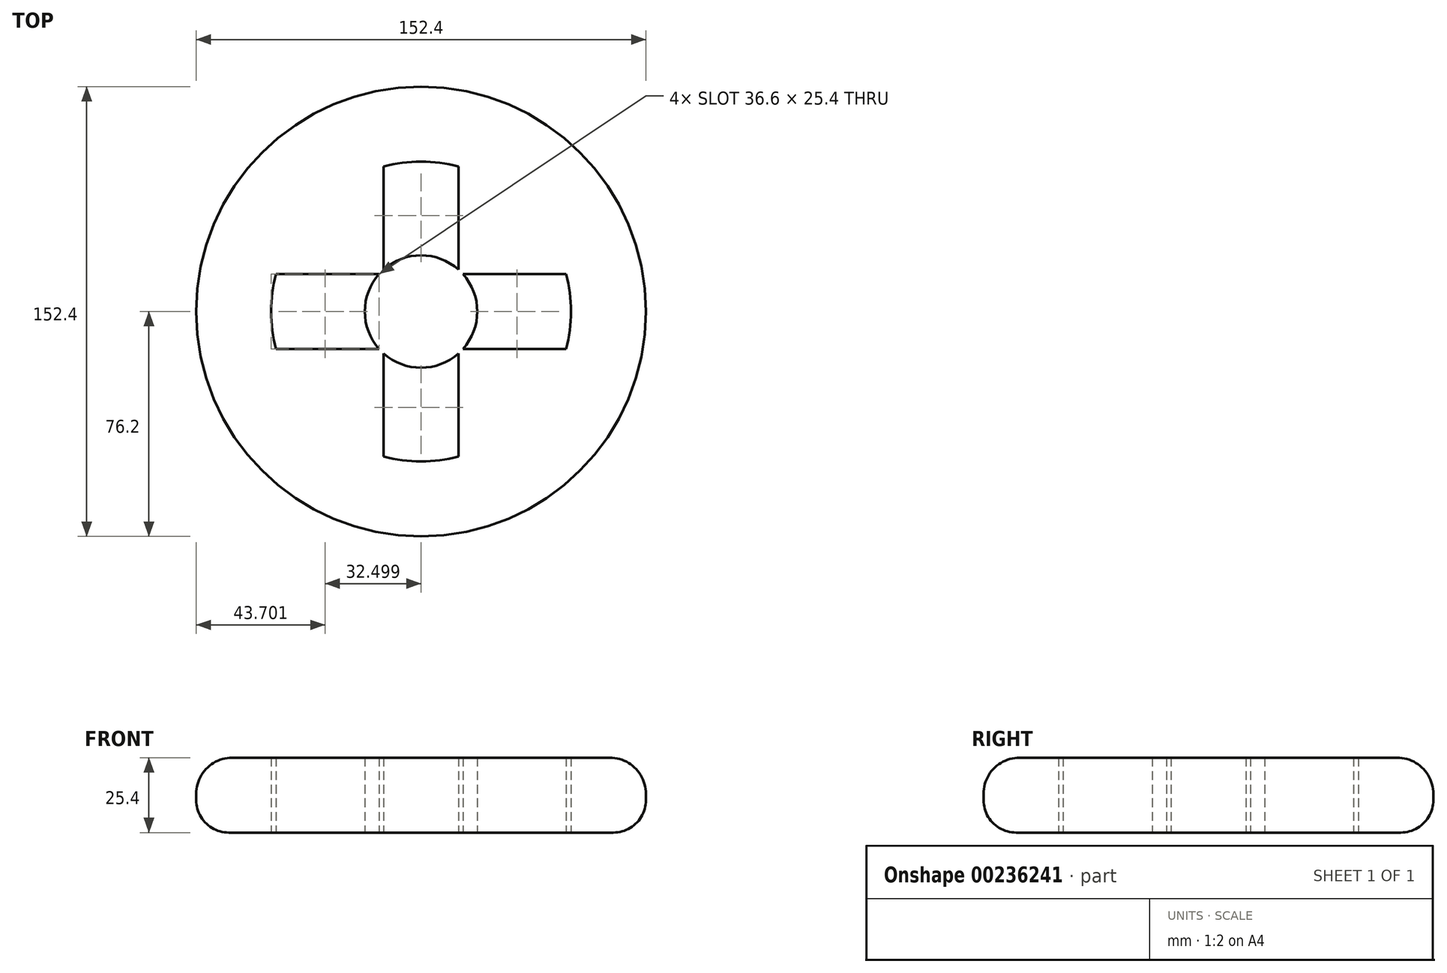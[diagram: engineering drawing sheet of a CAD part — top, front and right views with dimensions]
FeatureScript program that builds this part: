
annotation { "Feature Type Name" : "Feature", "Feature Type Description" : "" }
export const myFeature = defineFeature(function(context is Context, id is Id, definition is map)
    precondition{}
    {
        {
            var Q0;
            Q0=qCreatedBy(makeId("Top.planeOp"),FACE);
            var sketch = newSketch(context, id + "F0", { "sketchPlane" : qUnion([Q0])});
            skCircle(sketch, "E0", {"center": v(0, 0) * mm, "radius": 76.2 * mm});
            skCircle(sketch, "E1", {"center": v(0, 0) * mm, "radius": 50.8 * mm});
            skArc(sketch, "E2", {"start": v(14.2, -12.7) * mm, "mid": v(19.05, 0) * mm, "end": v(14.2, 12.7) * mm});
            skLineSegment(sketch, "E3", {"start": v(0, -50.8) * mm, "end": v(0, -12.7) * mm});
            skLineSegment(sketch, "E4.0", {"start": v(12.7, -49.19) * mm, "end": v(12.7, 0) * mm});
            skLineSegment(sketch, "E5.0", {"start": v(-12.7, -49.19) * mm, "end": v(-12.7, 0) * mm});
            skLineSegment(sketch, "E6", {"start": v(-12.7, 0) * mm, "end": v(-50.8, 0) * mm});
            skLineSegment(sketch, "E7", {"start": v(12.7, 0) * mm, "end": v(50.8, 0) * mm});
            skLineSegment(sketch, "E8", {"start": v(0, 12.7) * mm, "end": v(0, 50.8) * mm});
            skLineSegment(sketch, "E9.0", {"start": v(-12.7, 12.7) * mm, "end": v(-49.19, 12.7) * mm});
            skLineSegment(sketch, "E10.0", {"start": v(0, -12.7) * mm, "end": v(-49.19, -12.7) * mm});
            skLineSegment(sketch, "E10.1", {"start": v(0, -12.7) * mm, "end": v(49.19, -12.7) * mm});
            skLineSegment(sketch, "E11.0", {"start": v(0, 12.7) * mm, "end": v(49.19, 12.7) * mm});
            skLineSegment(sketch, "E12.0", {"start": v(12.7, 0) * mm, "end": v(12.7, 49.19) * mm});
            skLineSegment(sketch, "E13.0", {"start": v(-12.7, 12.7) * mm, "end": v(-12.7, 49.19) * mm});
            skLineSegment(sketch, "E14", {"start": v(-12.7, 12.7) * mm, "end": v(0, 12.7) * mm});
            skLineSegment(sketch, "E15", {"start": v(-12.7, 12.7) * mm, "end": v(-12.7, 0) * mm});
            skArc(sketch, "E16.trimOffspring", {"start": v(12.7, 14.2) * mm, "mid": v(0, 19.05) * mm, "end": v(-12.7, 14.2) * mm});
            skArc(sketch, "E17.trimOffspring", {"start": v(-14.2, 12.7) * mm, "mid": v(-19.05, 0) * mm, "end": v(-14.2, -12.7) * mm});
            skArc(sketch, "E18.trimOffspring", {"start": v(-12.7, -14.2) * mm, "mid": v(0, -19.05) * mm, "end": v(12.7, -14.2) * mm});
            skPoint(sketch, "E19.orphan", {"position": v(0, -76.2) * mm});
            skSolve(sketch);
        }
        {
            var Q0;
            Q0 = qSketchRegion(id + "F0", true);
            var Q1;
            {var subQ0=sQuery(id+"F0.wireOp",EDGE,"E4.0");var subQ1=sQuery(id+"F0.wireOp",EDGE,"E1");var subQ2=makeQuery(id+"F0.imprint","INTERSECT",VERTEX,{"derivedFrom":[subQ1,subQ0]});Q1=makeQuery(id+"F0.imprint","IMPRINT",FACE,{"disambiguationData":[TD([[makeQuery(id+"F0.imprint","IMPRINT",EDGE,{"disambiguationData":[TD([[subQ2,-1.0]])],"derivedFrom":subQ1}),1.0]])]});}
            var Q2;
            {var subQ0=sQuery(id+"F0.wireOp",EDGE,"E10.0");var subQ1=sQuery(id+"F0.wireOp",EDGE,"E1");var subQ2=makeQuery(id+"F0.imprint","INTERSECT",VERTEX,{"derivedFrom":[subQ1,subQ0]});Q2=makeQuery(id+"F0.imprint","IMPRINT",FACE,{"disambiguationData":[TD([[makeQuery(id+"F0.imprint","IMPRINT",EDGE,{"disambiguationData":[TD([[subQ2,-1.0]])],"derivedFrom":subQ1}),1.0]])]});}
            var Q3;
            {var subQ0=sQuery(id+"F0.wireOp",EDGE,"E13.0");var subQ1=sQuery(id+"F0.wireOp",EDGE,"E1");var subQ2=makeQuery(id+"F0.imprint","INTERSECT",VERTEX,{"derivedFrom":[subQ1,subQ0]});Q3=makeQuery(id+"F0.imprint","IMPRINT",FACE,{"disambiguationData":[TD([[makeQuery(id+"F0.imprint","IMPRINT",EDGE,{"disambiguationData":[TD([[subQ2,-1.0]])],"derivedFrom":subQ1}),1.0]])]});}
            var Q4;
            {var subQ0=sQuery(id+"F0.wireOp",EDGE,"E11.0");var subQ1=sQuery(id+"F0.wireOp",EDGE,"E1");var subQ2=makeQuery(id+"F0.imprint","INTERSECT",VERTEX,{"derivedFrom":[subQ1,subQ0]});Q4=makeQuery(id+"F0.imprint","IMPRINT",FACE,{"disambiguationData":[TD([[makeQuery(id+"F0.imprint","IMPRINT",EDGE,{"disambiguationData":[TD([[subQ2,-1.0]])],"derivedFrom":subQ1}),1.0]])]});}
            var Q5;
            {var subQ3=sQuery(id+"F0.wireOp",EDGE,"E10.1");var subQ5=sQuery(id+"F0.wireOp",EDGE,"E4.0");var subQ6=makeQuery(id+"F0.imprint","INTERSECT",VERTEX,{"derivedFrom":[subQ5,subQ3]});Q5=makeQuery(id+"F0.imprint","IMPRINT",FACE,{"disambiguationData":[TD([[makeQuery(id+"F0.imprint","IMPRINT",EDGE,{"disambiguationData":[TD([[subQ6,-1.0]])],"derivedFrom":subQ5}),1.0]])]});}
            var Q6;
            {var subQ3=sQuery(id+"F0.wireOp",EDGE,"E12.0");var subQ5=sQuery(id+"F0.wireOp",EDGE,"E11.0");var subQ7=makeQuery(id+"F0.imprint","INTERSECT",VERTEX,{"derivedFrom":[subQ5,subQ3]});Q6=makeQuery(id+"F0.imprint","IMPRINT",FACE,{"disambiguationData":[TD([[makeQuery(id+"F0.imprint","IMPRINT",EDGE,{"disambiguationData":[TD([[subQ7,1.0]])],"derivedFrom":subQ5}),-1.0]])]});}
            var Q7;
            {var subQ3=sQuery(id+"F0.wireOp",EDGE,"E13.0");var subQ5=sQuery(id+"F0.wireOp",EDGE,"E9.0");var subQ7=makeQuery(id+"F0.imprint","INTERSECT",VERTEX,{"derivedFrom":[subQ5,subQ3]});Q7=makeQuery(id+"F0.imprint","IMPRINT",FACE,{"disambiguationData":[TD([[makeQuery(id+"F0.imprint","IMPRINT",EDGE,{"disambiguationData":[TD([[subQ7,1.0]])],"derivedFrom":subQ5}),1.0]])]});}
            var Q8;
            {var subQ3=sQuery(id+"F0.wireOp",EDGE,"E10.0");var subQ5=sQuery(id+"F0.wireOp",EDGE,"E5.0");var subQ7=makeQuery(id+"F0.imprint","INTERSECT",VERTEX,{"derivedFrom":[subQ5,subQ3]});Q8=makeQuery(id+"F0.imprint","IMPRINT",FACE,{"disambiguationData":[TD([[makeQuery(id+"F0.imprint","IMPRINT",EDGE,{"disambiguationData":[TD([[subQ7,-1.0]])],"derivedFrom":subQ5}),-1.0]])]});}
            var Q9;
            {var subQ0=sQuery(id+"F0.wireOp",EDGE,"E5.0");var subQ1=sQuery(id+"F0.wireOp",EDGE,"E2");var subQ2=makeQuery(id+"F0.imprint","INTERSECT",VERTEX,{"derivedFrom":[subQ1,subQ0]});Q9=makeQuery(id+"F0.imprint","IMPRINT",FACE,{"disambiguationData":[TD([[makeQuery(id+"F0.imprint","IMPRINT",EDGE,{"disambiguationData":[TD([[subQ2,-1.0]])],"derivedFrom":subQ1}),1.0]])]});}
            var Q10;
            {var subQ0=sQuery(id+"F0.wireOp",EDGE,"E3");var subQ1=sQuery(id+"F0.wireOp",EDGE,"E2");var subQ2=makeQuery(id+"F0.imprint","INTERSECT",VERTEX,{"derivedFrom":[subQ1,subQ0]});Q10=makeQuery(id+"F0.imprint","IMPRINT",FACE,{"disambiguationData":[TD([[makeQuery(id+"F0.imprint","IMPRINT",EDGE,{"disambiguationData":[TD([[subQ2,-1.0]])],"derivedFrom":subQ1}),1.0]])]});}
            var Q11;
            {var subQ0=sQuery(id+"F0.wireOp",EDGE,"E7");var subQ1=sQuery(id+"F0.wireOp",EDGE,"E2");var subQ2=makeQuery(id+"F0.imprint","INTERSECT",VERTEX,{"derivedFrom":[subQ1,subQ0]});Q11=makeQuery(id+"F0.imprint","IMPRINT",FACE,{"disambiguationData":[TD([[makeQuery(id+"F0.imprint","IMPRINT",EDGE,{"disambiguationData":[TD([[subQ2,1.0]])],"derivedFrom":subQ1}),1.0]])]});}
            var Q12;
            {var subQ0=sQuery(id+"F0.wireOp",EDGE,"E11.0");var subQ1=sQuery(id+"F0.wireOp",EDGE,"E2");var subQ2=makeQuery(id+"F0.imprint","INTERSECT",VERTEX,{"derivedFrom":[subQ1,subQ0]});Q12=makeQuery(id+"F0.imprint","IMPRINT",FACE,{"disambiguationData":[TD([[makeQuery(id+"F0.imprint","IMPRINT",EDGE,{"disambiguationData":[TD([[subQ2,1.0]])],"derivedFrom":subQ1}),1.0]])]});}
            var Q13;
            {var subQ0=sQuery(id+"F0.wireOp",EDGE,"E12.0");var subQ1=sQuery(id+"F0.wireOp",EDGE,"E2");var subQ2=makeQuery(id+"F0.imprint","INTERSECT",VERTEX,{"derivedFrom":[subQ1,subQ0]});Q13=makeQuery(id+"F0.imprint","IMPRINT",FACE,{"disambiguationData":[TD([[makeQuery(id+"F0.imprint","IMPRINT",EDGE,{"disambiguationData":[TD([[subQ2,-1.0]])],"derivedFrom":subQ1}),1.0]])]});}
            var Q14;
            {var subQ0=sQuery(id+"F0.wireOp",EDGE,"E8");var subQ1=sQuery(id+"F0.wireOp",EDGE,"E2");var subQ2=makeQuery(id+"F0.imprint","INTERSECT",VERTEX,{"derivedFrom":[subQ1,subQ0]});Q14=makeQuery(id+"F0.imprint","IMPRINT",FACE,{"disambiguationData":[TD([[makeQuery(id+"F0.imprint","IMPRINT",EDGE,{"disambiguationData":[TD([[subQ2,-1.0]])],"derivedFrom":subQ1}),1.0]])]});}
            var Q15;
            {var subQ0=sQuery(id+"F0.wireOp",EDGE,"E9.0");var subQ1=sQuery(id+"F0.wireOp",EDGE,"E2");var subQ2=makeQuery(id+"F0.imprint","INTERSECT",VERTEX,{"derivedFrom":[subQ1,subQ0]});Q15=makeQuery(id+"F0.imprint","IMPRINT",FACE,{"disambiguationData":[TD([[makeQuery(id+"F0.imprint","IMPRINT",EDGE,{"disambiguationData":[TD([[subQ2,-1.0]])],"derivedFrom":subQ1}),1.0]])]});}
            var Q16;
            {var subQ0=sQuery(id+"F0.wireOp",EDGE,"E6");var subQ1=sQuery(id+"F0.wireOp",EDGE,"E2");var subQ2=makeQuery(id+"F0.imprint","INTERSECT",VERTEX,{"derivedFrom":[subQ1,subQ0]});Q16=makeQuery(id+"F0.imprint","IMPRINT",FACE,{"disambiguationData":[TD([[makeQuery(id+"F0.imprint","IMPRINT",EDGE,{"disambiguationData":[TD([[subQ2,-1.0]])],"derivedFrom":subQ1}),1.0]])]});}
            var Q17;
            {var subQ3=sQuery(id+"F0.wireOp",EDGE,"E18.trimOffspring");var subQ5=sQuery(id+"F0.wireOp",EDGE,"E4.0");var subQ6=makeQuery(id+"F0.imprint","INTERSECT",VERTEX,{"derivedFrom":[subQ5,subQ3]});Q17=makeQuery(id+"F0.imprint","IMPRINT",FACE,{"disambiguationData":[TD([[makeQuery(id+"F0.imprint","IMPRINT",EDGE,{"disambiguationData":[TD([[subQ6,-1.0]])],"derivedFrom":subQ5}),1.0]])]});}
            var Q18;
            {var subQ3=sQuery(id+"F0.wireOp",EDGE,"E18.trimOffspring");var subQ5=sQuery(id+"F0.wireOp",EDGE,"E5.0");var subQ6=makeQuery(id+"F0.imprint","INTERSECT",VERTEX,{"derivedFrom":[subQ5,subQ3]});Q18=makeQuery(id+"F0.imprint","IMPRINT",FACE,{"disambiguationData":[TD([[makeQuery(id+"F0.imprint","IMPRINT",EDGE,{"disambiguationData":[TD([[subQ6,-1.0]])],"derivedFrom":subQ5}),-1.0]])]});}
            var Q19;
            {var subQ3=sQuery(id+"F0.wireOp",EDGE,"E10.0");var subQ5=sQuery(id+"F0.wireOp",EDGE,"E17.trimOffspring");var subQ7=makeQuery(id+"F0.imprint","INTERSECT",VERTEX,{"derivedFrom":[subQ3,subQ5]});Q19=makeQuery(id+"F0.imprint","IMPRINT",FACE,{"disambiguationData":[TD([[makeQuery(id+"F0.imprint","IMPRINT",EDGE,{"disambiguationData":[TD([[subQ7,1.0]])],"derivedFrom":subQ3}),-1.0]])]});}
            var Q20;
            {var subQ0=sQuery(id+"F0.wireOp",EDGE,"E15");Q20=makeQuery(id+"F0.imprint","IMPRINT",FACE,{"disambiguationData":[TD([[makeQuery(id+"F0.imprint","IMPRINT",EDGE,{"derivedFrom":subQ0}),-1.0]])]});}
            var Q21;
            {var subQ0=sQuery(id+"F0.wireOp",EDGE,"E14");Q21=makeQuery(id+"F0.imprint","IMPRINT",FACE,{"disambiguationData":[TD([[makeQuery(id+"F0.imprint","IMPRINT",EDGE,{"derivedFrom":subQ0}),1.0]])]});}
            var Q22;
            {var subQ3=sQuery(id+"F0.wireOp",EDGE,"E16.trimOffspring");var subQ5=sQuery(id+"F0.wireOp",EDGE,"E12.0");var subQ7=makeQuery(id+"F0.imprint","INTERSECT",VERTEX,{"derivedFrom":[subQ5,subQ3]});Q22=makeQuery(id+"F0.imprint","IMPRINT",FACE,{"disambiguationData":[TD([[makeQuery(id+"F0.imprint","IMPRINT",EDGE,{"disambiguationData":[TD([[subQ7,1.0]])],"derivedFrom":subQ5}),1.0]])]});}
            extrude(context, id + "F1", {"entities" : qUnion([Q0, Q1, Q2, Q3, Q4, Q5, Q6, Q7, Q8, Q9, Q10, Q11, Q12, Q13, Q14, Q15, Q16, Q17, Q18, Q19, Q20, Q21, Q22]), "endBound" : BoundingType.SYMMETRIC, "depth" : 25.4 * mm});
        }
        {
            var Q0;
            Q0=makeQuery(id+"F1.opExtrude","CAP_EDGE",EDGE,{"disambiguationData":[OSD([sQuery(id+"F0.wireOp",EDGE,"E0")])],"isStart":false});
            fillet(context, id + "F2", {"entities" : qUnion([Q0]), "radius" : 12.26 * mm, "tangentPropagation" : true, "allowEdgeOverflow" : false});
        }
        {
            var Q0;
            Q0=makeQuery(id+"F1.opExtrude","CAP_EDGE",EDGE,{"disambiguationData":[OSD([sQuery(id+"F0.wireOp",EDGE,"E0")])],"isStart":true});
            fillet(context, id + "F3", {"entities" : qUnion([Q0]), "radius" : 11.04 * mm, "tangentPropagation" : true, "allowEdgeOverflow" : false});
        }
    });
